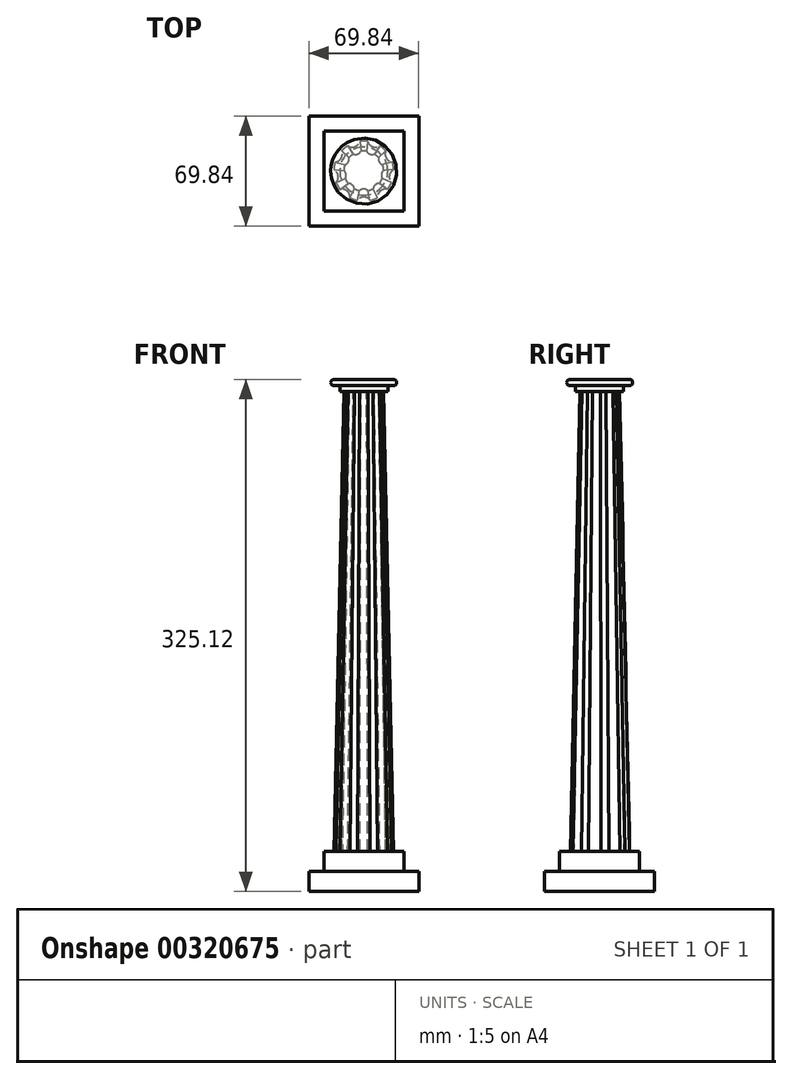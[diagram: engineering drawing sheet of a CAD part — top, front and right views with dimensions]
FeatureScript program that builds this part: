
annotation { "Feature Type Name" : "Feature", "Feature Type Description" : "" }
export const myFeature = defineFeature(function(context is Context, id is Id, definition is map)
    precondition{}
    {
        {
            var Q0;
            Q0=qCreatedBy(makeId("Top.planeOp"),FACE);
            var sketch = newSketch(context, id + "F0", { "sketchPlane" : qUnion([Q0])});
            skLineSegment(sketch, "E0.bottom", {"start": v(34.93, 34.93) * mm, "end": v(-34.92, 34.93) * mm});
            skLineSegment(sketch, "E0.top", {"start": v(34.92, -34.93) * mm, "end": v(-34.93, -34.93) * mm});
            skLineSegment(sketch, "E0.left", {"start": v(34.93, 34.93) * mm, "end": v(34.92, -34.92) * mm});
            skLineSegment(sketch, "E0.right", {"start": v(-34.92, 34.93) * mm, "end": v(-34.93, -34.93) * mm});
            skPoint(sketch, "E0.middle", {"position": v(0, 0) * mm});
            skSolve(sketch);
        }
        {
            var Q0;
            Q0=makeQuery(id+"F0.imprint","IMPRINT",FACE,{"disambiguationData":[TD([[makeQuery(id+"F0.imprint","IMPRINT",EDGE,{"derivedFrom":sQuery(id+"F0.wireOp",EDGE,"E0.bottom")}),1.0]])]});
            extrude(context, id + "F1", {"entities" : qUnion([Q0]), "depth" : 12.7 * mm});
        }
        {
            var Q0;
            Q0=makeQuery(id+"F1.opExtrude","CAP_FACE",FACE,{"disambiguationData":[OSD([sQuery(id+"F0.wireOp",EDGE,"E0.bottom"),sQuery(id+"F0.wireOp",EDGE,"E0.top"),sQuery(id+"F0.wireOp",EDGE,"E0.left"),sQuery(id+"F0.wireOp",EDGE,"E0.right")])],"isStart":false});
            var sketch = newSketch(context, id + "F2", { "sketchPlane" : qUnion([Q0])});
            skLineSegment(sketch, "E1.bottom", {"start": v(25.4, -25.4) * mm, "end": v(-25.4, -25.4) * mm});
            skLineSegment(sketch, "E1.top", {"start": v(25.4, 25.4) * mm, "end": v(-25.4, 25.4) * mm});
            skLineSegment(sketch, "E1.left", {"start": v(25.4, -25.4) * mm, "end": v(25.4, 25.4) * mm});
            skLineSegment(sketch, "E1.right", {"start": v(-25.4, -25.4) * mm, "end": v(-25.4, 25.4) * mm});
            skPoint(sketch, "E1.middle", {"position": v(0, 0) * mm});
            skSolve(sketch);
        }
        {
            var Q0;
            Q0=makeQuery(id+"F2.imprint","IMPRINT",FACE,{"disambiguationData":[TD([[makeQuery(id+"F2.imprint","IMPRINT",EDGE,{"derivedFrom":sQuery(id+"F2.wireOp",EDGE,"E1.bottom")}),-1.0]])]});
            extrude(context, id + "F3", {"entities" : qUnion([Q0]), "operationType" : NewBodyOperationType.ADD, "depth" : 12.7 * mm});
        }
        {
            var Q0;
            Q0=makeQuery(id+"F3.opExtrude","CAP_FACE",FACE,{"disambiguationData":[OSD([sQuery(id+"F2.wireOp",EDGE,"E1.bottom"),sQuery(id+"F2.wireOp",EDGE,"E1.top"),sQuery(id+"F2.wireOp",EDGE,"E1.left"),sQuery(id+"F2.wireOp",EDGE,"E1.right")])],"isStart":false});
            var sketch = newSketch(context, id + "F4", { "sketchPlane" : qUnion([Q0])});
            skCircle(sketch, "E2", {"center": v(0, 0) * mm, "radius": 19.05 * mm});
            skPoint(sketch, "E3", {"position": v(0, -21.59) * mm});
            skArc(sketch, "E4", {"start": v(4.1, -18.6) * mm, "mid": v(0, -16.51) * mm, "end": v(-4.1, -18.6) * mm});
            skArc(sketch, "E5.1.0", {"start": v(15.1, -11.6) * mm, "mid": v(10.61, -12.65) * mm, "end": v(8.8, -16.9) * mm});
            skArc(sketch, "E5.2.0", {"start": v(19.03, 0.82) * mm, "mid": v(16.26, -2.87) * mm, "end": v(17.6, -7.28) * mm});
            skArc(sketch, "E6.3.3.0", {"start": v(14.06, 12.86) * mm, "mid": v(14.3, 8.25) * mm, "end": v(18.16, 5.74) * mm});
            skArc(sketch, "E6.3.4.0", {"start": v(2.5, 18.89) * mm, "mid": v(5.65, 15.51) * mm, "end": v(10.22, 16.07) * mm});
            skArc(sketch, "E6.3.5.0", {"start": v(-10.22, 16.07) * mm, "mid": v(-5.65, 15.51) * mm, "end": v(-2.5, 18.89) * mm});
            skArc(sketch, "E6.3.6.0", {"start": v(-18.16, 5.74) * mm, "mid": v(-14.3, 8.26) * mm, "end": v(-14.06, 12.86) * mm});
            skArc(sketch, "E6.3.7.0", {"start": v(-17.6, -7.28) * mm, "mid": v(-16.26, -2.87) * mm, "end": v(-19.03, 0.82) * mm});
            skArc(sketch, "E6.3.8.0", {"start": v(-8.8, -16.9) * mm, "mid": v(-10.61, -12.65) * mm, "end": v(-15.1, -11.6) * mm});
            skSolve(sketch);
        }
        {
            var Q0;
            Q0=makeQuery(id+"F1.opExtrude","CAP_FACE",FACE,{"disambiguationData":[OSD([sQuery(id+"F0.wireOp",EDGE,"E0.bottom"),sQuery(id+"F0.wireOp",EDGE,"E0.top"),sQuery(id+"F0.wireOp",EDGE,"E0.left"),sQuery(id+"F0.wireOp",EDGE,"E0.right")])],"isStart":false});
            cPlane(context, id + "F5", {"entities" : qUnion([Q0]), "cplaneType" : CPlaneType.OFFSET, "offset" : 304.8 * mm, "width" : 152.4 * mm, "height" : 152.4 * mm});
        }
        {
            var Q0;
            Q0=qCreatedBy(id+"F5.planeOp",FACE);
            var sketch = newSketch(context, id + "F6", { "sketchPlane" : qUnion([Q0])});
            skCircle(sketch, "E7", {"center": v(0, 0) * mm, "radius": 12.7 * mm});
            skPoint(sketch, "E8", {"position": v(0, -15.24) * mm});
            skArc(sketch, "E9", {"start": v(2.58, -12.44) * mm, "mid": v(0, -11.43) * mm, "end": v(-2.58, -12.44) * mm});
            skArc(sketch, "E10.1.0", {"start": v(9.97, -7.87) * mm, "mid": v(7.35, -8.76) * mm, "end": v(6.02, -11.18) * mm});
            skArc(sketch, "E11.1.2.0", {"start": v(12.7, 0.38) * mm, "mid": v(11.26, -1.98) * mm, "end": v(11.8, -4.7) * mm});
            skArc(sketch, "E11.1.3.0", {"start": v(9.48, 8.45) * mm, "mid": v(9.9, 5.71) * mm, "end": v(12.06, 3.98) * mm});
            skArc(sketch, "E12.1.4.0", {"start": v(1.83, 12.57) * mm, "mid": v(3.9, 10.74) * mm, "end": v(6.68, 10.8) * mm});
            skArc(sketch, "E12.1.5.0", {"start": v(-6.68, 10.8) * mm, "mid": v(-3.9, 10.74) * mm, "end": v(-1.83, 12.57) * mm});
            skArc(sketch, "E12.1.6.0", {"start": v(-12.06, 3.98) * mm, "mid": v(-9.9, 5.72) * mm, "end": v(-9.48, 8.45) * mm});
            skArc(sketch, "E12.1.7.0", {"start": v(-11.8, -4.7) * mm, "mid": v(-11.26, -1.98) * mm, "end": v(-12.7, 0.38) * mm});
            skArc(sketch, "E12.1.8.0", {"start": v(-6.02, -11.18) * mm, "mid": v(-7.35, -8.76) * mm, "end": v(-9.97, -7.87) * mm});
            skSolve(sketch);
        }
        {
            var Q1;
            {var subQ0=sQuery(id+"F4.wireOp",EDGE,"E4");Q1=makeQuery(id+"F4.imprint","IMPRINT",FACE,{"disambiguationData":[TD([[makeQuery(id+"F4.imprint","IMPRINT",EDGE,{"derivedFrom":subQ0}),-1.0]])]});}
            var Q2;
            {var subQ0=sQuery(id+"F6.wireOp",EDGE,"E9");Q2=makeQuery(id+"F6.imprint","IMPRINT",FACE,{"disambiguationData":[TD([[makeQuery(id+"F6.imprint","IMPRINT",EDGE,{"derivedFrom":subQ0}),-1.0]])]});}
            loft(context, id + "F7", {"operationType" : NewBodyOperationType.ADD, "sheetProfilesArray" : [{ "sheetProfileEntities" : qUnion([Q1]) }, { "sheetProfileEntities" : qUnion([Q2]) }]});
        }
        {
            var Q0;
            Q0=qCreatedBy(makeId("Front.planeOp"),FACE);
            var sketch = newSketch(context, id + "F8", { "sketchPlane" : qUnion([Q0])});
            skLineSegment(sketch, "E13", {"start": v(0, 317.5) * mm, "end": v(0, 325.12) * mm});
            skLineSegment(sketch, "E14", {"start": v(0, 317.5) * mm, "end": v(15.24, 317.5) * mm});
            skLineSegment(sketch, "E15", {"start": v(0, 325.12) * mm, "end": v(19.05, 325.12) * mm});
            skLineSegment(sketch, "E16", {"start": v(15.24, 317.5) * mm, "end": v(15.24, 321.3) * mm});
            skLineSegment(sketch, "E17", {"start": v(15.24, 321.3) * mm, "end": v(19.05, 321.3) * mm});
            skLineSegment(sketch, "E18", {"start": v(19.05, 321.3) * mm, "end": v(19.05, 325.12) * mm});
            skArc(sketch, "E19", {"start": v(19.05, 321.3) * mm, "mid": v(20.95, 323.21) * mm, "end": v(19.05, 325.12) * mm});
            skSolve(sketch);
        }
        {
            var Q0;
            Q0=makeQuery(id+"F8.imprint","IMPRINT",FACE,{"disambiguationData":[TD([[makeQuery(id+"F8.imprint","IMPRINT",EDGE,{"derivedFrom":sQuery(id+"F8.wireOp",EDGE,"E13")}),-1.0]])]});
            var Q1;
            Q1=makeQuery(id+"F8.imprint","IMPRINT",FACE,{"disambiguationData":[TD([[makeQuery(id+"F8.imprint","IMPRINT",EDGE,{"derivedFrom":sQuery(id+"F8.wireOp",EDGE,"E18")}),-1.0]])]});
            var Q2;
            Q2=sQuery(id+"F8.wireOp",EDGE,"E13");
            revolve(context, id + "F9", {"operationType" : NewBodyOperationType.ADD, "entities" : qUnion([Q0, Q1]), "axis" : qUnion([Q2]), "revolveType" : RevolveType.FULL});
        }
    });
